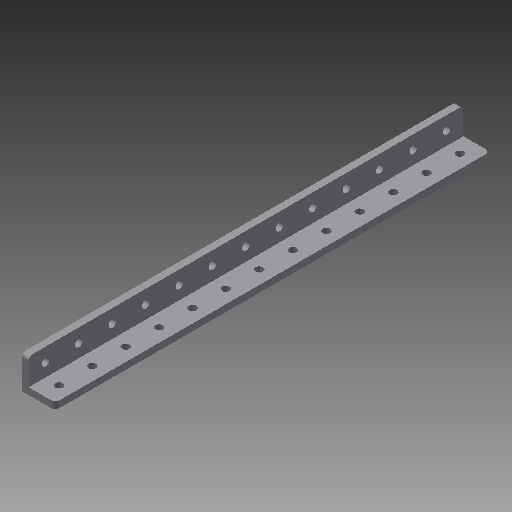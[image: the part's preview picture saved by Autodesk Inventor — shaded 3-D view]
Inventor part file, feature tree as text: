
AUTODESK INVENTOR PART (.ipt)
format: ipt  version: 2017 (Build 210142000, 142)  size: 160,768 bytes
history: native  units: in
note: dims shown in document units (in); Inventor stores cm internally (conversion verified against a paired STEP export)
features: other x1, imported_body x1, extrude x1, fillet x1, sketch x1
ambient origin geometry x8: Origin, YZ Plane, XZ Plane, XY Plane, X Axis, Y Axis, Z Axis, Center Point
bodies: Body1 (feature_tree)
feature tree (5):
  other  "ANGLE_288_2011"
  imported_body  "Base1"
  extrude  "Extrusion1"  Depth=0.0787in
  fillet  "Fillet1"  [1 undecoded]
  sketch  "Sketch1"  dims[d0=0.3937in d1=0.0in d2=0.0787in]
note: 1 required parameter value undecoded (feature->parameter linkage not recoverable at this tier; creation-order binding heuristic only, values carry confidence <= 0.55)
